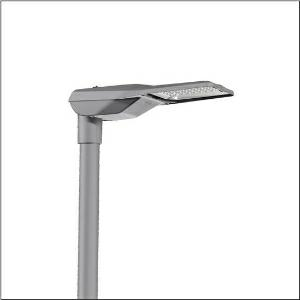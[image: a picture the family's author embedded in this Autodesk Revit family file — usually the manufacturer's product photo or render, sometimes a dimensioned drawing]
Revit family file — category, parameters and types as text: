
# Revit family: streetlight_sl_21_iq_mini___p0_8a_5xe2u31v08gb_4f31
name_source: partatom
category: Lighting Fixtures
units: mm (PartAtom-declared; Revit-internal decimal feet)

## family parameters
Cut with Voids When Loaded = No
Host = Face
Light Source = No
Part Type = Normal
Room Calculation Point = No
Round Connector Dimension = Use Diameter
Shared = No

## types (1)
- --- (1 x LED, 6040 lm, 39.8 W, 3000K)
    Apparent Load = 40 VA
    CIE Flux Codes = 33 69 96 100 100
    Color Rendering = 70
    Color Temperature = 3000K
    Default Elevation = 1800 mm
    Description = Streetlight SL 21 iQ mini, mast luminaire, primary light control with lens, of PMMA, primary optical cover: cover, of toughened safety glass, transparent, light distribution: P0.8a, light emission: direct distribution, primary light characteristic: asymmetric, installation type: post-top, side-entry, LED, High Power LED, rated luminous flux: 6.040lm, luminous efficacy: 152lm/W, light colour: 730, colour temperature: 3000K, control gear: iQ-Street Remote, D4i with power reduction, control: pre-setting: logarithmic dimming characteristic, Street-Remote, Auto-Match, Temp-Guard, Lumen-Switch, Night-Set, Smart-Wire, Light-Fading, Desk-Remote (wireless, voltage-free reading and setting of iQ features in the workshop via application-optimized NFC function/RFID function), optimised constant luminous flux control (CLO 2.0), mains connection: 220..240V, AC, 50/60Hz, start of lifetime: 40W, end of service life: 41W, reduction: 18W, luminaire housing, of diecast aluminium, powder-coated, Siteco® metallic grey (DB 702S), corrosivity category C5 mid according to DIN EN ISO 12944, please order mast flange separately, inclination adjustable: 0°, 5°, 10°, 15°, sealing non-destructively replaceable, multi-level sealing system, length: 628mm, width: 235mm, height: 110mm, mast flange for spigot size: 42mm (side-entry): 5XC10008XM4, 60/48mm (side-entry/post-top): 5XC10108XM2, 76/60mm (side-entry/post-top): 5XC10108XM1, mounting height: 4..8m, Smart Interface above, protection rating (complete): IP66, insulation class (complete): insulation class II (safety insulation), certification: CE, ENEC, ENEC+, VDE, impact resistance: IK10, permissible operating ambient temperature for outdoor applications: -40..+50°C, standard-compliant lighting for roads and squares, packaging unit: 1 piece

Light Distribution: P0.8a
    Height = 110 mm
    Lamp = 1 x LED
    Lamp Light Flux = 6040 lm
    Lamp Power = 39.8 W
    Lamp count = 1
    Length = 625 mm
    Luminous efficacy = 152 lm/W
    Manufacturer = Siteco
    ModVariant = No
    Model = 5XE2U31V08GB
    Number of Poles = 1
    OnlyDefault = Yes
    Power Factor = 1
    Product Name = Streetlight SL 21 iQ mini | P0.8a
    Product group = mast luminaire | pylon top
    ProductGroupID = 6100
    Protection Class = Protection class II
    Protection Degree = IP 66
    RLX_Detail_Level = 1
    RLX_Emergency_Light_Flux = 0 lm
    RLX_Emergency_Type = 0
    RLX_Emergency_Type_DB = No
    RlxData = <blob elided: 93285 chars, md5=fd929276>
    Socket = socket
    Standby Power = 0 W
    System Light Flux = 6040 lm
    System Power = 40 W
    Type Comments = factory setting: luminous flux: 100 % | dim-lin: 254 | 800 mA
    Type Image = l_1003515.jpg
    URL = http://relux.com
    VarID = @adj_095661
    Voltage = 0 V
    Weight = 0.00 kg
    Width = 234 mm

## geometry (parser evidence)
native form markers: Blend x4, Sweep x13
no freeform markers — native parametric forms only
